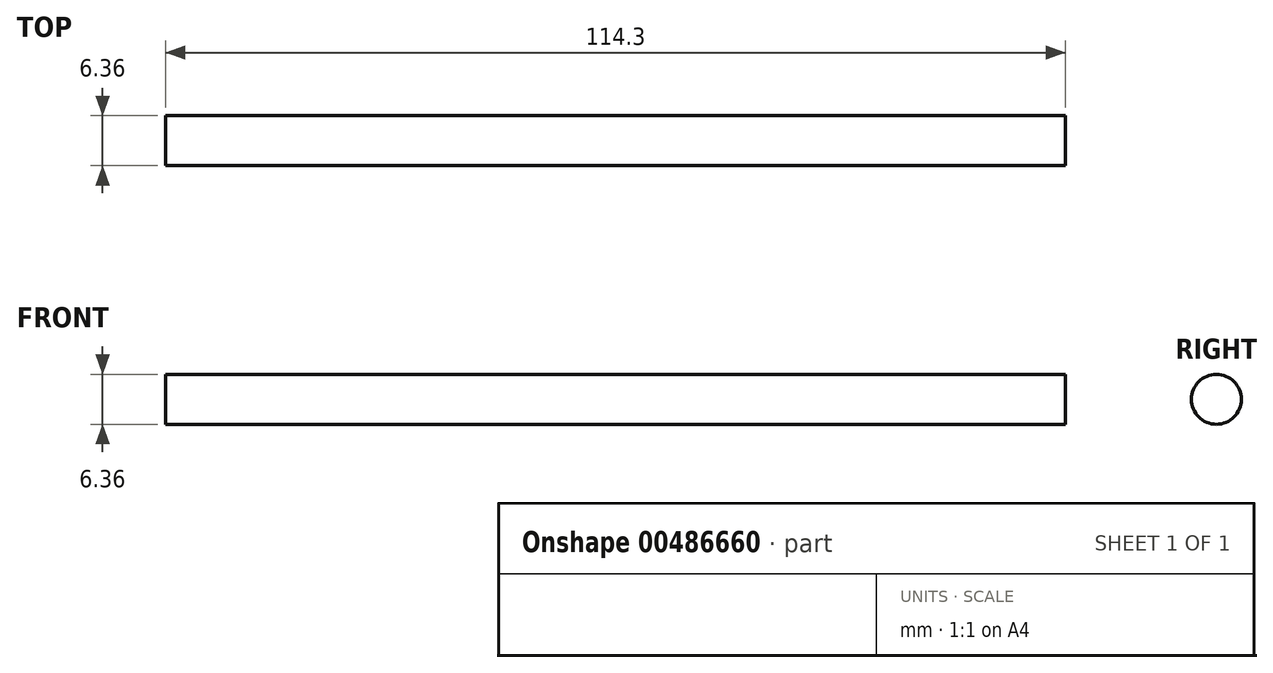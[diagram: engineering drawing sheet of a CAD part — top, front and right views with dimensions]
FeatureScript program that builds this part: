
annotation { "Feature Type Name" : "Feature", "Feature Type Description" : "" }
export const myFeature = defineFeature(function(context is Context, id is Id, definition is map)
    precondition{}
    {
        {
            var Q0;
            Q0=qCreatedBy(makeId("Top.planeOp"),FACE);
            var sketch = newSketch(context, id + "F0", { "sketchPlane" : qUnion([Q0])});
            skLineSegment(sketch, "E0.bottom", {"start": v(-57.15, 3.17) * mm, "end": v(57.15, 3.17) * mm});
            skLineSegment(sketch, "E0.top", {"start": v(-57.15, -3.17) * mm, "end": v(57.15, -3.17) * mm});
            skLineSegment(sketch, "E0.left", {"start": v(-57.15, 3.17) * mm, "end": v(-57.15, -3.17) * mm});
            skLineSegment(sketch, "E0.right", {"start": v(57.15, 3.17) * mm, "end": v(57.15, -3.17) * mm});
            skPoint(sketch, "E0.middle", {"position": v(0, 0) * mm});
            skLineSegment(sketch, "E1", {"start": v(-57.15, 0) * mm, "end": v(57.15, 0) * mm});
            skSolve(sketch);
        }
        {
            var Q0;
            Q0=makeQuery(id+"F0.imprint","IMPRINT",FACE,{"disambiguationData":[TD([[makeQuery(id+"F0.imprint","IMPRINT",EDGE,{"derivedFrom":sQuery(id+"F0.wireOp",EDGE,"E0.bottom")}),-1.0]])]});
            var Q1;
            Q1=sQuery(id+"F0.wireOp",EDGE,"E1");
            revolve(context, id + "F1", {"entities" : qUnion([Q0]), "axis" : qUnion([Q1]), "revolveType" : RevolveType.FULL});
        }
    });
